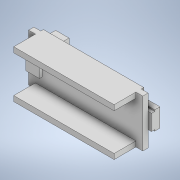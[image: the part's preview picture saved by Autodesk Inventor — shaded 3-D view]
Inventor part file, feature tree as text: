
AUTODESK INVENTOR PART (.ipt)
format: ipt  version: 2022 (Build 260153070, 153G)  size: 159,744 bytes
history: native  units: mm
features: extrude x4, sketch x3
ambient origin geometry x8: Origin, YZ Plane, XZ Plane, XY Plane, X Axis, Y Axis, Z Axis, Center Point
bodies: Solid1 (feature_tree)
feature tree (7):
  sketch  "Sketch1"  dims[d0=43.25mm d1=18.0mm]
  extrude  "Extrusion1"  Depth=18.0mm
  extrude  "Extrusion2"  Depth=5.08mm
  extrude  "Extrusion3"  Depth=3.0mm TaperAngle=0.0deg
  extrude  "Extrusion4"  Depth=6.0mm
  sketch  "Sketch2"  dims[d3=7.62mm d4=5.08mm]
  sketch  "Sketch3"  dims[d5=2.0mm d6=0.0mm d7=3.0mm d8=0.0mm d9=6.0mm d10=1.25mm d12=7.0mm d13=2.0mm d14=1.25mm d15=8.0mm d16=0.0mm d17=0.0mm d18=8.25mm d19=0.0mm d20=38.0mm d21=2.0mm d22=8.25mm d23=3.0mm d24=0.0mm d25=0.0mm]
